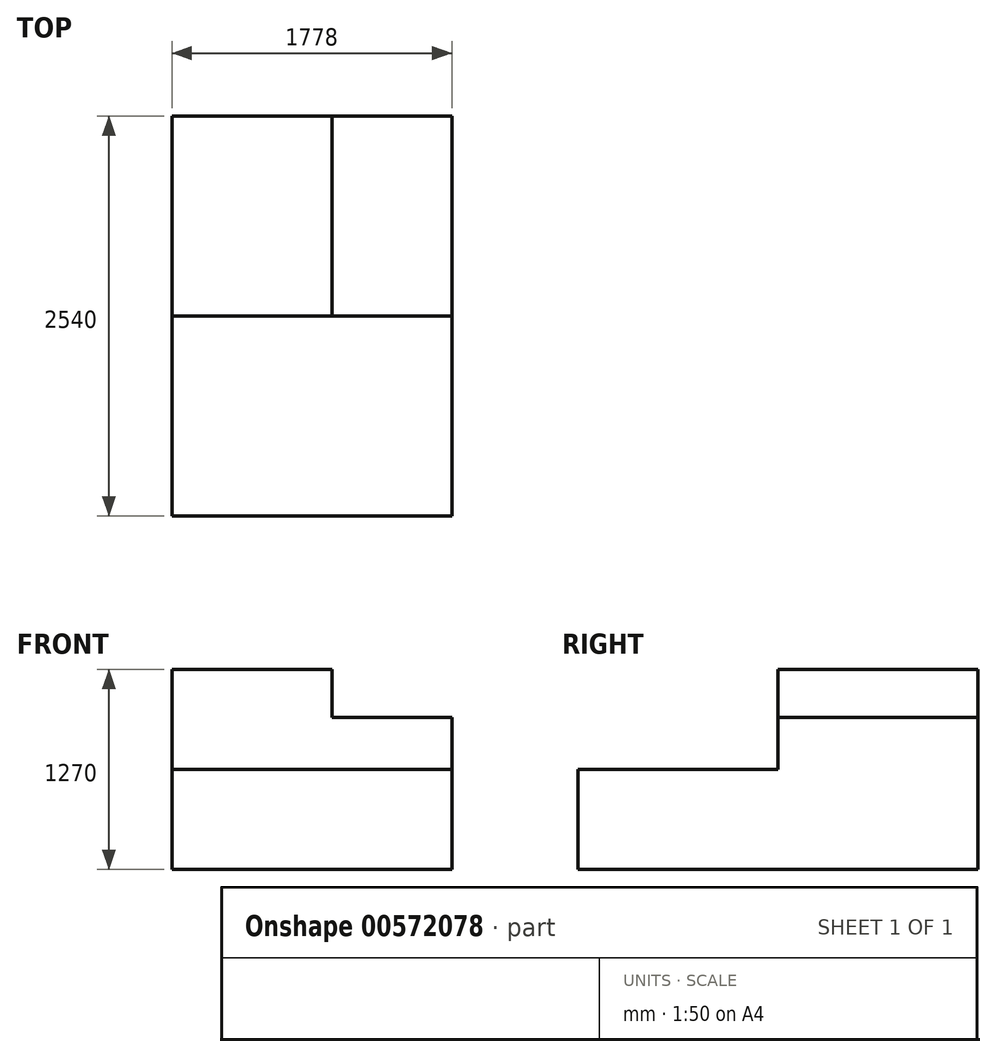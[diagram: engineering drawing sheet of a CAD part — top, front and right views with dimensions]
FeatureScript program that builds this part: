
annotation { "Feature Type Name" : "Feature", "Feature Type Description" : "" }
export const myFeature = defineFeature(function(context is Context, id is Id, definition is map)
    precondition{}
    {
        {
            var Q0;
            Q0=qCreatedBy(makeId("Right.planeOp"),FACE);
            var sketch = newSketch(context, id + "F0", { "sketchPlane" : qUnion([Q0])});
            skLineSegment(sketch, "E0", {"start": v(0, 0) * mm, "end": v(2540, 0) * mm});
            skLineSegment(sketch, "E1", {"start": v(2540, 0) * mm, "end": v(2540, 965.2) * mm});
            skLineSegment(sketch, "E2", {"start": v(2540, 965.2) * mm, "end": v(2540, 1270) * mm});
            skLineSegment(sketch, "E3", {"start": v(2540, 1270) * mm, "end": v(1270, 1270) * mm});
            skLineSegment(sketch, "E4", {"start": v(1270, 1270) * mm, "end": v(1270, 635) * mm});
            skLineSegment(sketch, "E5", {"start": v(1270, 635) * mm, "end": v(0, 635) * mm});
            skLineSegment(sketch, "E6", {"start": v(0, 635) * mm, "end": v(0, 0) * mm});
            skLineSegment(sketch, "E7", {"start": v(2540, 965.2) * mm, "end": v(1270, 965.2) * mm});
            skSolve(sketch);
        }
        {
            var Q0;
            Q0=makeQuery(id+"F0.imprint","IMPRINT",FACE,{"disambiguationData":[TD([[makeQuery(id+"F0.imprint","IMPRINT",EDGE,{"derivedFrom":sQuery(id+"F0.wireOp",EDGE,"E0")}),1.0]])]});
            extrude(context, id + "F1", {"entities" : qUnion([Q0]), "depth" : 1778 * mm, "offsetDistance" : 25.4 * mm});
        }
        {
            var Q0;
            Q0 = qSketchRegion(id + "F0", true);
            extrude(context, id + "F2", {"entities" : qUnion([Q0]), "operationType" : NewBodyOperationType.ADD, "depth" : 1016 * mm, "offsetDistance" : 25.4 * mm});
        }
    });
